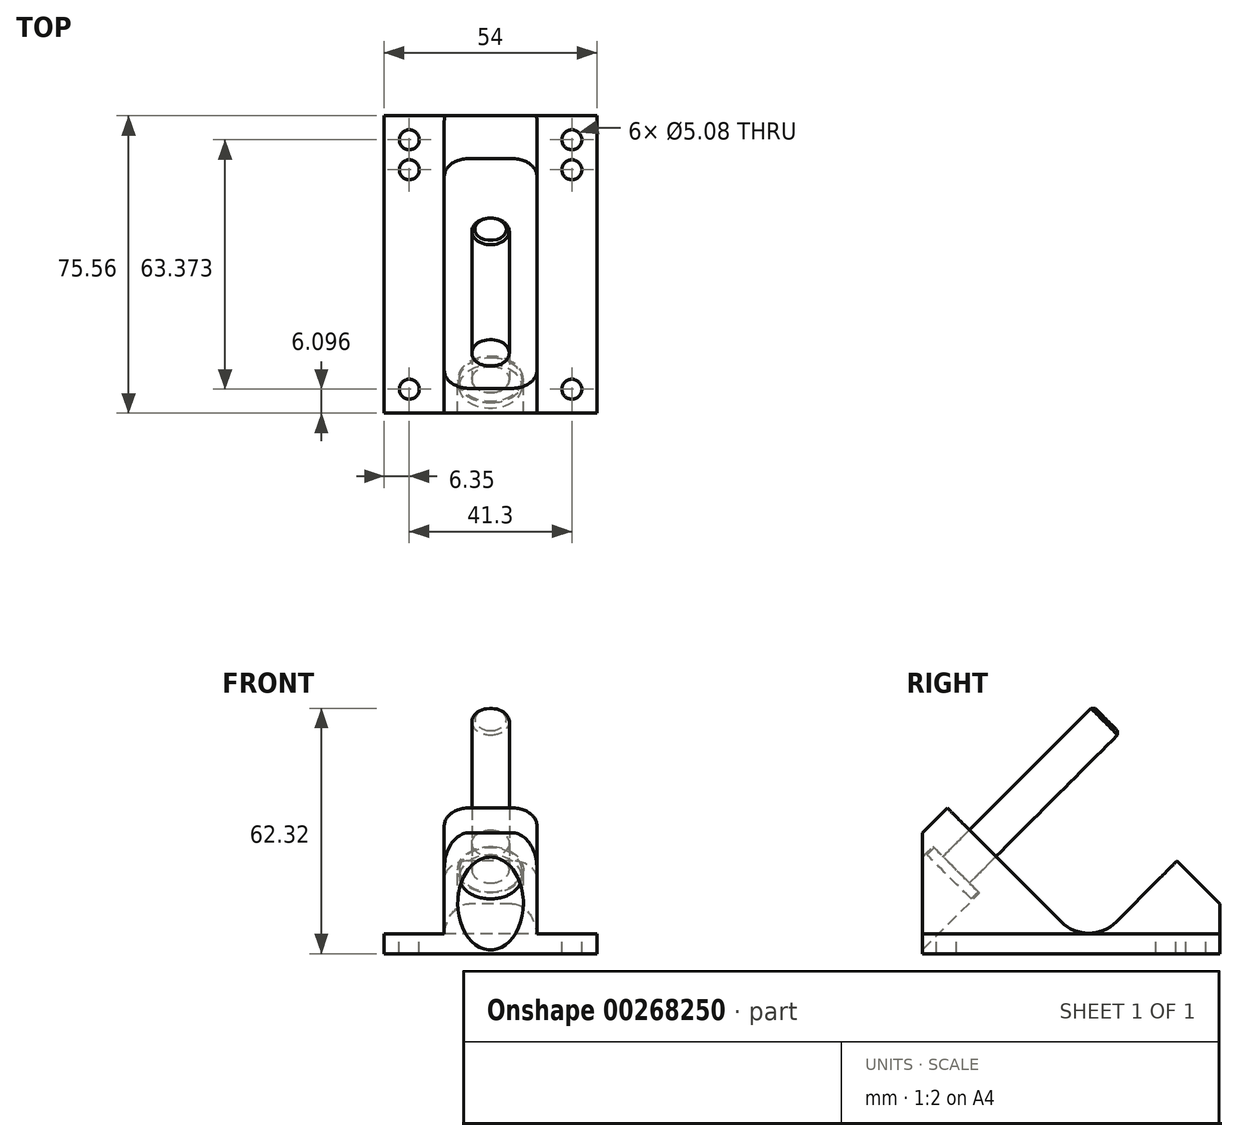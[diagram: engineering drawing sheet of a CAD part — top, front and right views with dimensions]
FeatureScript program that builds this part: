
annotation { "Feature Type Name" : "Feature", "Feature Type Description" : "" }
export const myFeature = defineFeature(function(context is Context, id is Id, definition is map)
    precondition{}
    {
        {
            var Q0;
            Q0=qCreatedBy(makeId("Right.planeOp"),FACE);
            var sketch = newSketch(context, id + "F0", { "sketchPlane" : qUnion([Q0])});
            skLineSegment(sketch, "E0", {"start": v(0, 0) * mm, "end": v(0, 30.72) * mm});
            skLineSegment(sketch, "E1", {"start": v(0, 30.72) * mm, "end": v(6.32, 37.04) * mm});
            skLineSegment(sketch, "E2", {"start": v(6.32, 37.04) * mm, "end": v(42.25, 1.12) * mm});
            skLineSegment(sketch, "E3", {"start": v(42.25, 1.12) * mm, "end": v(64.7, 23.57) * mm});
            skLineSegment(sketch, "E4", {"start": v(64.7, 23.57) * mm, "end": v(75.57, 12.7) * mm});
            skLineSegment(sketch, "E5", {"start": v(75.57, 12.7) * mm, "end": v(75.57, 0) * mm});
            skLineSegment(sketch, "E6", {"start": v(75.57, 0) * mm, "end": v(0, 0) * mm});
            skLineSegment(sketch, "E7", {"start": v(15.3, 28.06) * mm, "end": v(28.77, 41.53) * mm, "construction": true});
            skLineSegment(sketch, "E8", {"start": v(28.77, 41.53) * mm, "end": v(55.72, 14.59) * mm, "construction": true});
            skLineSegment(sketch, "E9", {"start": v(55.72, 14.59) * mm, "end": v(64.7, 5.6) * mm, "construction": true});
            skLineSegment(sketch, "E10", {"start": v(64.7, 5.6) * mm, "end": v(70.08, 11) * mm, "construction": true});
            skLineSegment(sketch, "E11", {"start": v(70.08, 11) * mm, "end": v(61.1, 19.98) * mm, "construction": true});
            skLineSegment(sketch, "E12", {"start": v(28.77, 41.53) * mm, "end": v(15.3, 55) * mm, "construction": true});
            skCircle(sketch, "E13", {"center": v(15.3, 55) * mm, "radius": 4 * mm, "construction": true});
            skLineSegment(sketch, "E14", {"start": v(64.7, 5.6) * mm, "end": v(59.3, 0.22) * mm, "construction": true});
            skLineSegment(sketch, "E15", {"start": v(59.3, 0.22) * mm, "end": v(50.33, 9.2) * mm, "construction": true});
            skCircle(sketch, "E16", {"center": v(58.4, 11.9) * mm, "radius": 5.08 * mm, "construction": true});
            skSolve(sketch);
        }
        {
            var Q0;
            Q0=qSketchRegion(id+"F0",true);
            extrude(context, id + "F1", {"entities" : qUnion([Q0]), "depth" : 27 * mm});
        }
        {
            var Q0;
            Q0=makeQuery(id+"F1.opExtrude","SWEPT_EDGE",EDGE,{"disambiguationData":[OSD([sQuery(id+"F0.wireOp",EDGE,"E2"),sQuery(id+"F0.wireOp",EDGE,"E3")])]});
            fillet(context, id + "F2", {"entities" : qUnion([Q0]), "radius" : 9.9 * mm, "tangentPropagation" : true, "allowEdgeOverflow" : false});
        }
        {
            var Q0;
            Q0=makeQuery(id+"F1.opExtrude","CAP_FACE",FACE,{"disambiguationData":[OSD([sQuery(id+"F0.wireOp",EDGE,"E0"),sQuery(id+"F0.wireOp",EDGE,"E1"),sQuery(id+"F0.wireOp",EDGE,"E2"),sQuery(id+"F0.wireOp",EDGE,"E3"),sQuery(id+"F0.wireOp",EDGE,"E4"),sQuery(id+"F0.wireOp",EDGE,"E5"),sQuery(id+"F0.wireOp",EDGE,"E6")])],"isStart":false});
            var sketch = newSketch(context, id + "F3", { "sketchPlane" : qUnion([Q0])});
            skLineSegment(sketch, "E17.bottom", {"start": v(0, 5.08) * mm, "end": v(75.57, 5.08) * mm});
            skLineSegment(sketch, "E17.top", {"start": v(0, 37.04) * mm, "end": v(75.57, 37.04) * mm});
            skLineSegment(sketch, "E17.left", {"start": v(0, 5.08) * mm, "end": v(0, 37.04) * mm});
            skLineSegment(sketch, "E17.right", {"start": v(75.57, 5.08) * mm, "end": v(75.57, 37.04) * mm});
            skSolve(sketch);
        }
        {
            var Q0;
            Q0=qSketchRegion(id+"F3",true);
            extrude(context, id + "F4", {"entities" : qUnion([Q0]), "operationType" : NewBodyOperationType.REMOVE, "oppositeDirection" : true, "depth" : 15.24 * mm});
        }
        {
            var Q0;
            Q0=makeQuery(id+"F4.boolean.opBoolean","COPY",FACE,{"derivedFrom":makeQuery(id+"F4.opExtrude","SWEPT_FACE",FACE,{"disambiguationData":[OSD([sQuery(id+"F3.wireOp",EDGE,"E17.bottom")])]})});
            var sketch = newSketch(context, id + "F5", { "sketchPlane" : qUnion([Q0])});
            skLineSegment(sketch, "E18", {"start": v(20.65, 69.47) * mm, "end": v(20.65, 61.85) * mm, "construction": true});
            skLineSegment(sketch, "E19", {"start": v(20.65, 61.85) * mm, "end": v(20.65, 6.1) * mm, "construction": true});
            skCircle(sketch, "E20", {"center": v(20.65, 69.47) * mm, "radius": 2.54 * mm});
            skCircle(sketch, "E21", {"center": v(20.65, 61.85) * mm, "radius": 2.54 * mm});
            skCircle(sketch, "E22", {"center": v(20.65, 6.1) * mm, "radius": 2.54 * mm});
            skSolve(sketch);
        }
        {
            var Q0;
            Q0=qSketchRegion(id+"F5",true);
            extrude(context, id + "F6", {"entities" : qUnion([Q0]), "operationType" : NewBodyOperationType.REMOVE, "endBound" : BoundingType.THROUGH_ALL, "oppositeDirection" : true, "depth" : 25.4 * mm});
        }
        {
            var Q0;
            Q0=makeQuery(id+"F1.opExtrude","SWEPT_BODY",BODY,{"disambiguationData":[OSD([sQuery(id+"F0.wireOp",EDGE,"E0"),sQuery(id+"F0.wireOp",EDGE,"E1"),sQuery(id+"F0.wireOp",EDGE,"E2"),sQuery(id+"F0.wireOp",EDGE,"E3"),sQuery(id+"F0.wireOp",EDGE,"E4"),sQuery(id+"F0.wireOp",EDGE,"E5"),sQuery(id+"F0.wireOp",EDGE,"E6")])]});
            var Q1;
            Q1=makeQuery(id+"F1.opExtrude","CAP_FACE",FACE,{"disambiguationData":[OSD([sQuery(id+"F0.wireOp",EDGE,"E0"),sQuery(id+"F0.wireOp",EDGE,"E1"),sQuery(id+"F0.wireOp",EDGE,"E2"),sQuery(id+"F0.wireOp",EDGE,"E3"),sQuery(id+"F0.wireOp",EDGE,"E4"),sQuery(id+"F0.wireOp",EDGE,"E5"),sQuery(id+"F0.wireOp",EDGE,"E6")])],"isStart":true});
            mirror(context, id + "F7", {"operationType" : NewBodyOperationType.ADD, "entities" : qUnion([Q0]), "mirrorPlane" : qUnion([Q1])});
        }
        {
            var Q0;
            Q0=makeQuery(id+"F7.opPattern","COPY",EDGE,{"derivedFrom":makeQuery(id+"F4.boolean.opBoolean","INTERSECT",EDGE,{"derivedFrom":[makeQuery(id+"F1.opExtrude","SWEPT_FACE",FACE,{"disambiguationData":[OSD([sQuery(id+"F0.wireOp",EDGE,"E1")])]}),makeQuery(id+"F4.opExtrude","CAP_FACE",FACE,{"disambiguationData":[OSD([sQuery(id+"F3.wireOp",EDGE,"E17.bottom"),sQuery(id+"F3.wireOp",EDGE,"E17.top"),sQuery(id+"F3.wireOp",EDGE,"E17.left"),sQuery(id+"F3.wireOp",EDGE,"E17.right")])],"isStart":false})]}),"instanceName":"1"});
            var Q1;
            Q1=makeQuery(id+"F4.boolean.opBoolean","INTERSECT",EDGE,{"derivedFrom":[makeQuery(id+"F1.opExtrude","SWEPT_FACE",FACE,{"disambiguationData":[OSD([sQuery(id+"F0.wireOp",EDGE,"E1")])]}),makeQuery(id+"F4.opExtrude","CAP_FACE",FACE,{"disambiguationData":[OSD([sQuery(id+"F3.wireOp",EDGE,"E17.bottom"),sQuery(id+"F3.wireOp",EDGE,"E17.top"),sQuery(id+"F3.wireOp",EDGE,"E17.left"),sQuery(id+"F3.wireOp",EDGE,"E17.right")])],"isStart":false})]});
            var Q2;
            Q2=makeQuery(id+"F7.opPattern","COPY",EDGE,{"derivedFrom":makeQuery(id+"F4.boolean.opBoolean","INTERSECT",EDGE,{"derivedFrom":[makeQuery(id+"F1.opExtrude","SWEPT_FACE",FACE,{"disambiguationData":[OSD([sQuery(id+"F0.wireOp",EDGE,"E4")])]}),makeQuery(id+"F4.opExtrude","CAP_FACE",FACE,{"disambiguationData":[OSD([sQuery(id+"F3.wireOp",EDGE,"E17.bottom"),sQuery(id+"F3.wireOp",EDGE,"E17.top"),sQuery(id+"F3.wireOp",EDGE,"E17.left"),sQuery(id+"F3.wireOp",EDGE,"E17.right")])],"isStart":false})]}),"instanceName":"1"});
            var Q3;
            Q3=makeQuery(id+"F4.boolean.opBoolean","INTERSECT",EDGE,{"derivedFrom":[makeQuery(id+"F1.opExtrude","SWEPT_FACE",FACE,{"disambiguationData":[OSD([sQuery(id+"F0.wireOp",EDGE,"E4")])]}),makeQuery(id+"F4.opExtrude","CAP_FACE",FACE,{"disambiguationData":[OSD([sQuery(id+"F3.wireOp",EDGE,"E17.bottom"),sQuery(id+"F3.wireOp",EDGE,"E17.top"),sQuery(id+"F3.wireOp",EDGE,"E17.left"),sQuery(id+"F3.wireOp",EDGE,"E17.right")])],"isStart":false})]});
            fillet(context, id + "F8", {"entities" : qUnion([Q0, Q1, Q2, Q3]), "radius" : 6.35 * mm, "tangentPropagation" : true, "allowEdgeOverflow" : false});
        }
        {
            var Q0;
            Q0=qCreatedBy(makeId("Right.planeOp"),FACE);
            var sketch = newSketch(context, id + "F9", { "sketchPlane" : qUnion([Q0])});
            skLineSegment(sketch, "E23.0", {"start": v(15.3, 28.06) * mm, "end": v(28.77, 41.53) * mm, "construction": true});
            skLineSegment(sketch, "E23.1", {"start": v(6.32, 37.04) * mm, "end": v(42.25, 1.12) * mm, "construction": true});
            skLineSegment(sketch, "E24", {"start": v(15.3, 28.06) * mm, "end": v(11.94, 31.43) * mm});
            skLineSegment(sketch, "E25", {"start": v(11.94, 31.43) * mm, "end": v(5.2, 24.7) * mm});
            skLineSegment(sketch, "E26", {"start": v(5.2, 24.7) * mm, "end": v(2.67, 27.22) * mm});
            skLineSegment(sketch, "E27", {"start": v(2.67, 27.22) * mm, "end": v(-12.28, 12.28) * mm});
            skLineSegment(sketch, "E28", {"start": v(-12.28, 12.28) * mm, "end": v(-6.38, 6.38) * mm});
            skLineSegment(sketch, "E29", {"start": v(-6.38, 6.38) * mm, "end": v(15.3, 28.06) * mm});
            skLineSegment(sketch, "E30", {"start": v(-6.38, 6.38) * mm, "end": v(0, 0) * mm, "construction": true});
            skSolve(sketch);
        }
        {
            var Q0;
            Q0=qSketchRegion(id+"F9",true);
            var Q1;
            Q1=sQuery(id+"F9.wireOp",EDGE,"E23.0");
            revolve(context, id + "F10", {"operationType" : NewBodyOperationType.REMOVE, "entities" : qUnion([Q0]), "axis" : qUnion([Q1]), "revolveType" : RevolveType.FULL, "oppositeDirection" : true});
        }
        {
            var Q0;
            Q0=qCreatedBy(makeId("Right.planeOp"),FACE);
            var sketch = newSketch(context, id + "F11", { "sketchPlane" : qUnion([Q0])});
            skLineSegment(sketch, "E31.1", {"start": v(5.2, 24.7) * mm, "end": v(2.96, 26.94) * mm});
            skLineSegment(sketch, "E31.2", {"start": v(11.94, 31.43) * mm, "end": v(5.2, 24.7) * mm});
            skLineSegment(sketch, "E32", {"start": v(2.96, 26.94) * mm, "end": v(1.16, 25.14) * mm});
            skPoint(sketch, "E31.0.end.orphan", {"position": v(-12.28, 12.28) * mm});
            skPoint(sketch, "E31.0.start.orphan", {"position": v(2.67, 27.22) * mm});
            skLineSegment(sketch, "E33", {"start": v(1.16, 25.14) * mm, "end": v(6.77, 19.53) * mm});
            skLineSegment(sketch, "E34", {"start": v(6.77, 19.53) * mm, "end": v(46.74, 59.5) * mm});
            skLineSegment(sketch, "E35", {"start": v(46.74, 59.5) * mm, "end": v(43.37, 62.86) * mm});
            skLineSegment(sketch, "E36", {"start": v(43.37, 62.86) * mm, "end": v(11.94, 31.43) * mm});
            skSolve(sketch);
        }
        {
            var Q0;
            Q0=qSketchRegion(id+"F11",true);
            var Q1;
            Q1=sQuery(id+"F11.wireOp",EDGE,"E34");
            revolve(context, id + "F12", {"entities" : qUnion([Q0]), "axis" : qUnion([Q1]), "revolveType" : RevolveType.FULL});
        }
        {
            var Q0;
            Q0=makeQuery(id+"F12.opRevolve","SWEPT_EDGE",EDGE,{"disambiguationData":[OSD([sQuery(id+"F11.wireOp",EDGE,"E35"),sQuery(id+"F11.wireOp",EDGE,"E36")])]});
            chamfer(context, id + "F13", {"entities" : qUnion([Q0]), "width" : 0.76 * mm, "tangentPropagation" : true});
        }
    });
